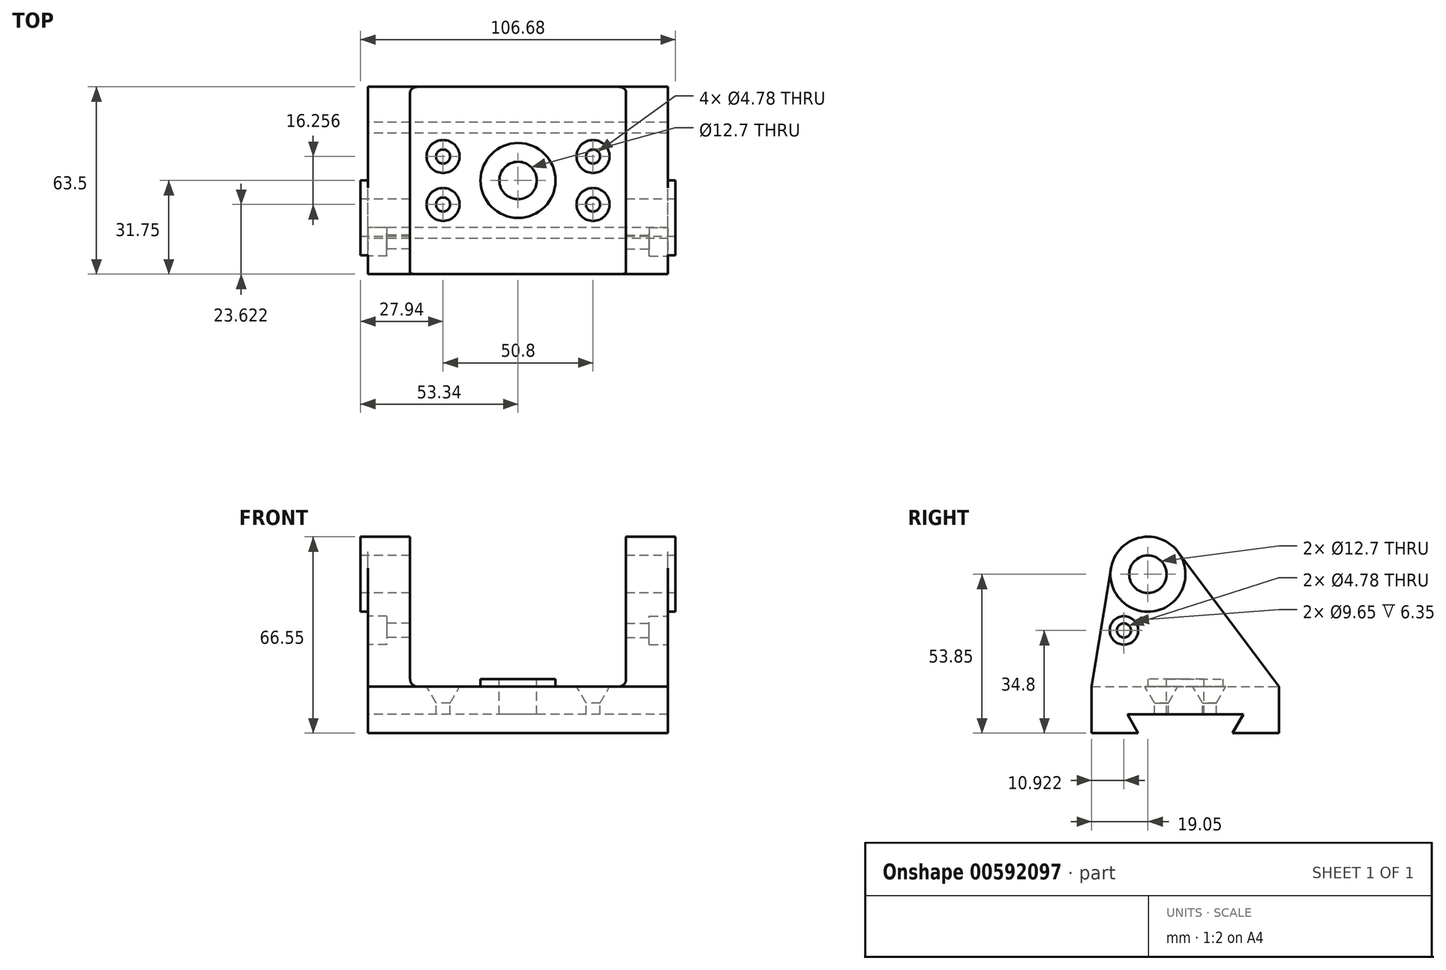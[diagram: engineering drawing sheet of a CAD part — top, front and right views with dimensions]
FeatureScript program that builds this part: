
annotation { "Feature Type Name" : "Feature", "Feature Type Description" : "" }
export const myFeature = defineFeature(function(context is Context, id is Id, definition is map)
    precondition{}
    {
        {
            var Q0;
            Q0=qCreatedBy(makeId("Right.planeOp"),FACE);
            var sketch = newSketch(context, id + "F0", { "sketchPlane" : qUnion([Q0])});
            skLineSegment(sketch, "E0", {"start": v(-51.47, 0) * mm, "end": v(52.9, 0) * mm, "construction": true});
            skLineSegment(sketch, "E1", {"start": v(0, 51.27) * mm, "end": v(0, -51.47) * mm, "construction": true});
            skCircle(sketch, "E2", {"center": v(-12.7, 38.1) * mm, "radius": 12.7 * mm});
            skCircle(sketch, "E3", {"center": v(-12.7, 38.1) * mm, "radius": 6.35 * mm});
            skLineSegment(sketch, "E4", {"start": v(-25.24, 40.13) * mm, "end": v(-31.75, 0) * mm});
            skLineSegment(sketch, "E5", {"start": v(-31.75, 0) * mm, "end": v(-31.75, -15.75) * mm});
            skLineSegment(sketch, "E6", {"start": v(-31.75, -15.75) * mm, "end": v(-16, -15.75) * mm});
            skLineSegment(sketch, "E7", {"start": v(-16, -15.75) * mm, "end": v(-19.67, -9.4) * mm});
            skLineSegment(sketch, "E8", {"start": v(-19.67, -9.4) * mm, "end": v(19.67, -9.4) * mm});
            skLineSegment(sketch, "E9", {"start": v(19.67, -9.4) * mm, "end": v(16, -15.75) * mm});
            skLineSegment(sketch, "E10", {"start": v(16, -15.75) * mm, "end": v(31.75, -15.75) * mm});
            skLineSegment(sketch, "E11", {"start": v(31.75, -15.75) * mm, "end": v(31.75, 0) * mm});
            skLineSegment(sketch, "E12", {"start": v(31.75, 0) * mm, "end": v(-2.54, 45.72) * mm});
            skLineSegment(sketch, "E13", {"start": v(-31.75, 0) * mm, "end": v(31.75, 0) * mm});
            skPoint(sketch, "E14", {"position": v(0, -9.4) * mm});
            skSolve(sketch);
        }
        {
            var Q0;
            Q0 = qSketchRegion(id + "F0", true);
            extrude(context, id + "F1", {"entities" : qUnion([Q0]), "endBound" : BoundingType.SYMMETRIC, "depth" : 101.6 * mm, "offsetDistance" : 25.4 * mm});
        }
        {
            var Q0;
            Q0=makeQuery(id+"F0.imprint","IMPRINT",FACE,{"disambiguationData":[TD([[makeQuery(id+"F0.imprint","IMPRINT",EDGE,{"derivedFrom":sQuery(id+"F0.wireOp",EDGE,"E3")}),-1.0]])]});
            extrude(context, id + "F2", {"entities" : qUnion([Q0]), "operationType" : NewBodyOperationType.ADD, "endBound" : BoundingType.SYMMETRIC, "depth" : 106.68 * mm, "offsetDistance" : 25.4 * mm});
        }
        {
            var Q0;
            {var subQ0=sQuery(id+"F0.wireOp",EDGE,"E4");Q0=makeQuery(id+"F0.imprint","IMPRINT",FACE,{"disambiguationData":[TD([[makeQuery(id+"F0.imprint","IMPRINT",EDGE,{"derivedFrom":subQ0}),1.0]])]});}
            var Q1;
            Q1=makeQuery(id+"F0.imprint","IMPRINT",FACE,{"disambiguationData":[TD([[makeQuery(id+"F0.imprint","IMPRINT",EDGE,{"derivedFrom":sQuery(id+"F0.wireOp",EDGE,"E3")}),-1.0]])]});
            extrude(context, id + "F3", {"entities" : qUnion([Q0, Q1]), "operationType" : NewBodyOperationType.REMOVE, "endBound" : BoundingType.SYMMETRIC, "oppositeDirection" : true, "depth" : 73.15 * mm, "offsetDistance" : 25.4 * mm});
        }
        {
            var Q0;
            Q0=makeQuery(id+"F3.boolean.opBoolean","COPY",FACE,{"derivedFrom":makeQuery(id+"F3.opExtrude","SWEPT_FACE",FACE,{"disambiguationData":[OSD([sQuery(id+"F0.wireOp",EDGE,"E13")])]})});
            var sketch = newSketch(context, id + "F4", { "sketchPlane" : qUnion([Q0])});
            skCircle(sketch, "E15", {"center": v(0, 0) * mm, "radius": 6.35 * mm});
            skCircle(sketch, "E16", {"center": v(0, 0) * mm, "radius": 12.7 * mm});
            skPoint(sketch, "E17", {"position": v(-25.4, 8.13) * mm});
            skLineSegment(sketch, "E18", {"start": v(-51.24, 0) * mm, "end": v(85.97, 0) * mm, "construction": true});
            skPoint(sketch, "E18.endSnap0", {"position": v(-36.58, 0) * mm});
            skPoint(sketch, "E19.MirrorP", {"position": v(-25.4, -8.13) * mm});
            skPoint(sketch, "E20.MirrorP", {"position": v(25.4, 8.13) * mm});
            skLineSegment(sketch, "E21", {"start": v(0, 34.17) * mm, "end": v(0, -42.92) * mm, "construction": true});
            skPoint(sketch, "E22.MirrorP", {"position": v(25.4, -8.13) * mm});
            skSolve(sketch);
        }
        {
            var Q0;
            Q0=sQuery(id+"F4.wireOp",VERTEX,"E17");
            var Q1;
            Q1=sQuery(id+"F4.wireOp",VERTEX,"E19.MirrorP");
            var Q2;
            Q2=sQuery(id+"F4.wireOp",VERTEX,"E20.MirrorP");
            var Q3;
            Q3=sQuery(id+"F4.wireOp",VERTEX,"E22.MirrorP");
            var Q4;
            Q4=makeQuery(id+"F1.opExtrude","SWEPT_BODY",BODY,{"disambiguationData":[OSD([sQuery(id+"F0.wireOp",EDGE,"E2"),sQuery(id+"F0.wireOp",EDGE,"E3"),sQuery(id+"F0.wireOp",EDGE,"E4"),sQuery(id+"F0.wireOp",EDGE,"E5"),sQuery(id+"F0.wireOp",EDGE,"E6"),sQuery(id+"F0.wireOp",EDGE,"E7"),sQuery(id+"F0.wireOp",EDGE,"E8"),sQuery(id+"F0.wireOp",EDGE,"E9"),sQuery(id+"F0.wireOp",EDGE,"E10"),sQuery(id+"F0.wireOp",EDGE,"E11"),sQuery(id+"F0.wireOp",EDGE,"E12")])]});
            hole(context, id + "F5", {"style" : HoleStyle.C_SINK, "endStyle" : HoleEndStyle.THROUGH, "holeDiameter" : 4.78 * mm, "cSinkDiameter" : 11.18 * mm, "cSinkAngle" : 60 * degree, "majorDiameter" : 6.35 * mm, "isTappedThrough" : true, "tappedDepth" : 12.7 * mm, "tapClearance" : 3, "locations" : qUnion([Q0, Q1, Q2, Q3]), "scope" : qUnion([Q4])});
        }
        {
            var Q0;
            Q0=makeQuery(id+"F4.imprint","IMPRINT",FACE,{"disambiguationData":[TD([[makeQuery(id+"F4.imprint","IMPRINT",EDGE,{"derivedFrom":sQuery(id+"F4.wireOp",EDGE,"E15")}),1.0]])]});
            extrude(context, id + "F6", {"entities" : qUnion([Q0]), "operationType" : NewBodyOperationType.REMOVE, "oppositeDirection" : true, "depth" : 25.4 * mm, "offsetDistance" : 25.4 * mm});
        }
        {
            var Q0;
            Q0=makeQuery(id+"F4.imprint","IMPRINT",FACE,{"disambiguationData":[TD([[makeQuery(id+"F4.imprint","IMPRINT",EDGE,{"derivedFrom":sQuery(id+"F4.wireOp",EDGE,"E15")}),-1.0]])]});
            extrude(context, id + "F7", {"entities" : qUnion([Q0]), "operationType" : NewBodyOperationType.ADD, "depth" : 2.54 * mm, "offsetDistance" : 25.4 * mm});
        }
        {
            var Q0;
            Q0=makeQuery(id+"F7.opExtrude","CAP_EDGE",EDGE,{"disambiguationData":[OSD([sQuery(id+"F4.wireOp",EDGE,"E16")])],"isStart":true});
            var Q1;
            Q1=makeQuery(id+"F3.boolean.opBoolean","COPY",EDGE,{"derivedFrom":makeQuery(id+"F3.opExtrude","CAP_EDGE",EDGE,{"disambiguationData":[OSD([sQuery(id+"F0.wireOp",EDGE,"E13")])],"isStart":true})});
            var Q2;
            Q2=makeQuery(id+"F3.boolean.opBoolean","COPY",EDGE,{"derivedFrom":makeQuery(id+"F3.opExtrude","CAP_EDGE",EDGE,{"disambiguationData":[OSD([sQuery(id+"F0.wireOp",EDGE,"E13")])],"isStart":false})});
            fillet(context, id + "F8", {"entities" : qUnion([Q0, Q1, Q2]), "radius" : 2.54 * mm, "tangentPropagation" : true, "allowEdgeOverflow" : false});
        }
        {
            var Q0;
            Q0=makeQuery(id+"F1.opExtrude","CAP_FACE",FACE,{"disambiguationData":[OSD([sQuery(id+"F0.wireOp",EDGE,"E2"),sQuery(id+"F0.wireOp",EDGE,"E3"),sQuery(id+"F0.wireOp",EDGE,"E4"),sQuery(id+"F0.wireOp",EDGE,"E5"),sQuery(id+"F0.wireOp",EDGE,"E6"),sQuery(id+"F0.wireOp",EDGE,"E7"),sQuery(id+"F0.wireOp",EDGE,"E8"),sQuery(id+"F0.wireOp",EDGE,"E9"),sQuery(id+"F0.wireOp",EDGE,"E10"),sQuery(id+"F0.wireOp",EDGE,"E11"),sQuery(id+"F0.wireOp",EDGE,"E12")])],"isStart":false});
            var sketch = newSketch(context, id + "F9", { "sketchPlane" : qUnion([Q0])});
            skPoint(sketch, "E23", {"position": v(-20.83, 19.05) * mm});
            skSolve(sketch);
        }
        {
            var Q0;
            Q0=sQuery(id+"F9.wireOp",VERTEX,"E23");
            var Q1;
            Q1=makeQuery(id+"F1.opExtrude","SWEPT_BODY",BODY,{"disambiguationData":[OSD([sQuery(id+"F0.wireOp",EDGE,"E2"),sQuery(id+"F0.wireOp",EDGE,"E3"),sQuery(id+"F0.wireOp",EDGE,"E4"),sQuery(id+"F0.wireOp",EDGE,"E5"),sQuery(id+"F0.wireOp",EDGE,"E6"),sQuery(id+"F0.wireOp",EDGE,"E7"),sQuery(id+"F0.wireOp",EDGE,"E8"),sQuery(id+"F0.wireOp",EDGE,"E9"),sQuery(id+"F0.wireOp",EDGE,"E10"),sQuery(id+"F0.wireOp",EDGE,"E11"),sQuery(id+"F0.wireOp",EDGE,"E12")])]});
            hole(context, id + "F10", {"style" : HoleStyle.C_BORE, "endStyle" : HoleEndStyle.BLIND, "holeDiameter" : 4.78 * mm, "cBoreDiameter" : 9.65 * mm, "cBoreDepth" : 6.35 * mm, "majorDiameter" : 6.35 * mm, "holeDepth" : 25.4 * mm, "isTappedThrough" : true, "tappedDepth" : 12.7 * mm, "tapClearance" : 3, "locations" : qUnion([Q0]), "scope" : qUnion([Q1])});
        }
        {
            var Q0;
            Q0=makeQuery(id+"F1.opExtrude","CAP_FACE",FACE,{"disambiguationData":[OSD([sQuery(id+"F0.wireOp",EDGE,"E2"),sQuery(id+"F0.wireOp",EDGE,"E3"),sQuery(id+"F0.wireOp",EDGE,"E4"),sQuery(id+"F0.wireOp",EDGE,"E5"),sQuery(id+"F0.wireOp",EDGE,"E6"),sQuery(id+"F0.wireOp",EDGE,"E7"),sQuery(id+"F0.wireOp",EDGE,"E8"),sQuery(id+"F0.wireOp",EDGE,"E9"),sQuery(id+"F0.wireOp",EDGE,"E10"),sQuery(id+"F0.wireOp",EDGE,"E11"),sQuery(id+"F0.wireOp",EDGE,"E12")])],"isStart":true});
            var sketch = newSketch(context, id + "F11", { "sketchPlane" : qUnion([Q0])});
            skPoint(sketch, "E24.0", {"position": v(20.83, 19.05) * mm});
            skSolve(sketch);
        }
        {
            var Q0;
            Q0=sQuery(id+"F11.wireOp",VERTEX,"E24.0");
            var Q1;
            Q1=makeQuery(id+"F1.opExtrude","SWEPT_BODY",BODY,{"disambiguationData":[OSD([sQuery(id+"F0.wireOp",EDGE,"E2"),sQuery(id+"F0.wireOp",EDGE,"E3"),sQuery(id+"F0.wireOp",EDGE,"E4"),sQuery(id+"F0.wireOp",EDGE,"E5"),sQuery(id+"F0.wireOp",EDGE,"E6"),sQuery(id+"F0.wireOp",EDGE,"E7"),sQuery(id+"F0.wireOp",EDGE,"E8"),sQuery(id+"F0.wireOp",EDGE,"E9"),sQuery(id+"F0.wireOp",EDGE,"E10"),sQuery(id+"F0.wireOp",EDGE,"E11"),sQuery(id+"F0.wireOp",EDGE,"E12")])]});
            hole(context, id + "F12", {"style" : HoleStyle.C_BORE, "endStyle" : HoleEndStyle.BLIND, "holeDiameter" : 4.78 * mm, "cBoreDiameter" : 9.65 * mm, "cBoreDepth" : 6.35 * mm, "majorDiameter" : 6.35 * mm, "holeDepth" : 25.4 * mm, "isTappedThrough" : true, "tappedDepth" : 12.7 * mm, "tapClearance" : 3, "locations" : qUnion([Q0]), "scope" : qUnion([Q1])});
        }
    });
